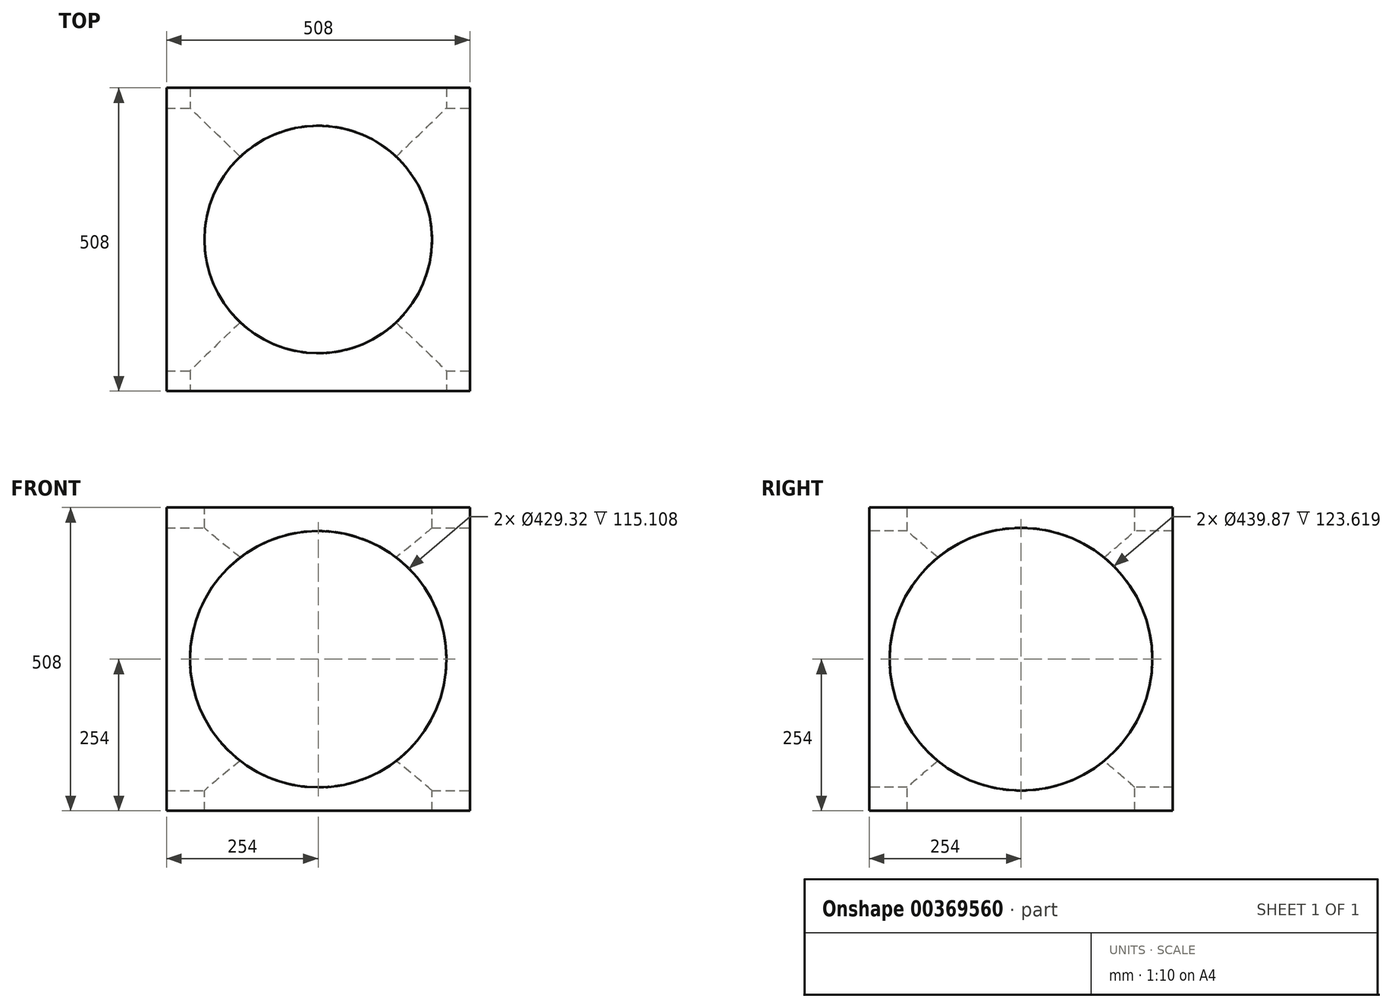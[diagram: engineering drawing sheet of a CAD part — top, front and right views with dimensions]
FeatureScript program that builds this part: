
annotation { "Feature Type Name" : "Feature", "Feature Type Description" : "" }
export const myFeature = defineFeature(function(context is Context, id is Id, definition is map)
    precondition{}
    {
        {
            var Q0;
            Q0=qCreatedBy(makeId("Top.planeOp"),FACE);
            var sketch = newSketch(context, id + "F0", { "sketchPlane" : qUnion([Q0])});
            skLineSegment(sketch, "E0.bottom", {"start": v(254, 254) * mm, "end": v(-254, 254) * mm});
            skLineSegment(sketch, "E0.top", {"start": v(254, -254) * mm, "end": v(-254, -254) * mm});
            skLineSegment(sketch, "E0.left", {"start": v(254, 254) * mm, "end": v(254, -254) * mm});
            skLineSegment(sketch, "E0.right", {"start": v(-254, 254) * mm, "end": v(-254, -254) * mm});
            skPoint(sketch, "E0.middle", {"position": v(0, 0) * mm});
            skSolve(sketch);
        }
        {
            var Q0;
            Q0 = qSketchRegion(id + "F0", true);
            extrude(context, id + "F1", {"entities" : qUnion([Q0]), "depth" : 508 * mm});
        }
        {
            var Q0;
            Q0=makeQuery(id+"F1.opExtrude","CAP_FACE",FACE,{"disambiguationData":[OSD([sQuery(id+"F0.wireOp",EDGE,"E0.bottom"),sQuery(id+"F0.wireOp",EDGE,"E0.top"),sQuery(id+"F0.wireOp",EDGE,"E0.left"),sQuery(id+"F0.wireOp",EDGE,"E0.right")])],"isStart":false});
            var sketch = newSketch(context, id + "F2", { "sketchPlane" : qUnion([Q0])});
            skCircle(sketch, "E1", {"center": v(0, 0) * mm, "radius": 190.5 * mm});
            skSolve(sketch);
        }
        {
            var Q0;
            Q0=makeQuery(id+"F2.imprint","IMPRINT",FACE,{"disambiguationData":[TD([[makeQuery(id+"F2.imprint","IMPRINT",EDGE,{"derivedFrom":sQuery(id+"F2.wireOp",EDGE,"E1")}),1.0]])]});
            extrude(context, id + "F3", {"entities" : qUnion([Q0]), "operationType" : NewBodyOperationType.REMOVE, "endBound" : BoundingType.UP_TO_NEXT, "oppositeDirection" : true, "depth" : 25.4 * mm});
        }
        {
            var Q0;
            Q0=makeQuery(id+"F1.opExtrude","SWEPT_FACE",FACE,{"disambiguationData":[OSD([sQuery(id+"F0.wireOp",EDGE,"E0.top")])]});
            var sketch = newSketch(context, id + "F4", { "sketchPlane" : qUnion([Q0])});
            skCircle(sketch, "E2", {"center": v(0, 254) * mm, "radius": 214.66 * mm});
            skPoint(sketch, "E2.centerSnap0", {"position": v(254, 254) * mm});
            skSolve(sketch);
        }
        {
            var Q0;
            Q0=makeQuery(id+"F4.imprint","IMPRINT",FACE,{"disambiguationData":[TD([[makeQuery(id+"F4.imprint","IMPRINT",EDGE,{"derivedFrom":sQuery(id+"F4.wireOp",EDGE,"E2")}),1.0]])]});
            extrude(context, id + "F5", {"entities" : qUnion([Q0]), "operationType" : NewBodyOperationType.REMOVE, "oppositeDirection" : true, "depth" : 558.8 * mm});
        }
        {
            var Q0;
            Q0=makeQuery(id+"F1.opExtrude","SWEPT_FACE",FACE,{"disambiguationData":[OSD([sQuery(id+"F0.wireOp",EDGE,"E0.left")])]});
            var sketch = newSketch(context, id + "F6", { "sketchPlane" : qUnion([Q0])});
            skCircle(sketch, "E3", {"center": v(0, 254) * mm, "radius": 219.93 * mm});
            skPoint(sketch, "E3.centerSnap0", {"position": v(254, 254) * mm});
            skSolve(sketch);
        }
        {
            var Q0;
            Q0=makeQuery(id+"F6.imprint","IMPRINT",FACE,{"disambiguationData":[TD([[makeQuery(id+"F6.imprint","IMPRINT",EDGE,{"derivedFrom":sQuery(id+"F6.wireOp",EDGE,"E3")}),1.0]])]});
            extrude(context, id + "F7", {"entities" : qUnion([Q0]), "operationType" : NewBodyOperationType.REMOVE, "oppositeDirection" : true, "depth" : 558.8 * mm});
        }
    });
